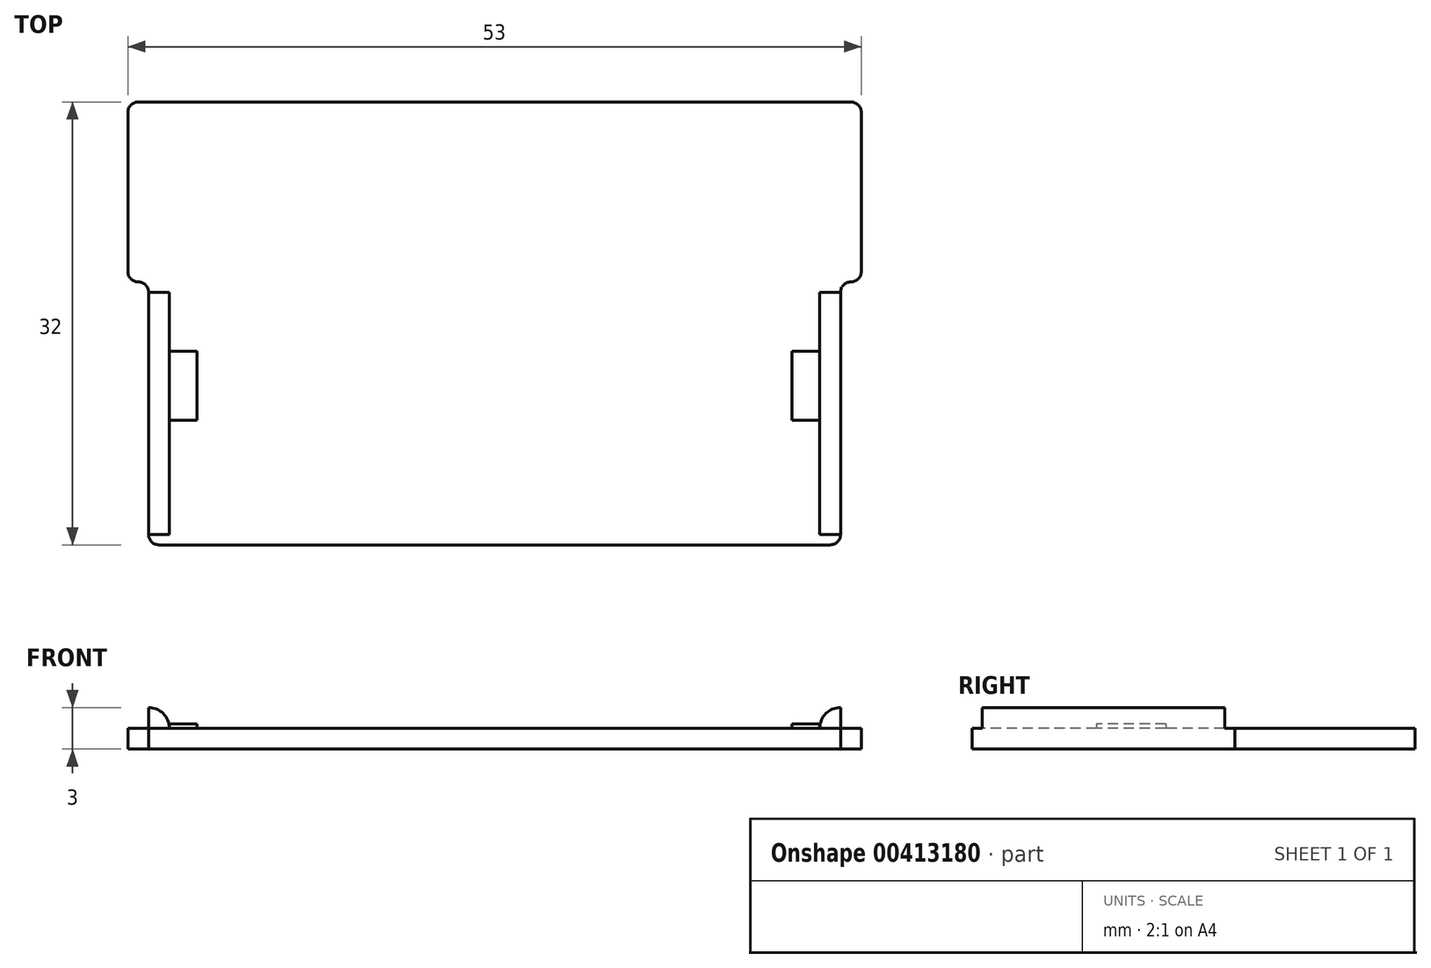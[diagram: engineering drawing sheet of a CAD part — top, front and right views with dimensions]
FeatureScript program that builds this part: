
annotation { "Feature Type Name" : "Feature", "Feature Type Description" : "" }
export const myFeature = defineFeature(function(context is Context, id is Id, definition is map)
    precondition{}
    {
        {
            var Q0;
            Q0=qCreatedBy(makeId("Top.planeOp"),FACE);
            var sketch = newSketch(context, id + "F0", { "sketchPlane" : qUnion([Q0])});
            skLineSegment(sketch, "E0.bottom", {"start": v(-25, 16) * mm, "end": v(25, 16) * mm});
            skLineSegment(sketch, "E0.top", {"start": v(-25, -16) * mm, "end": v(25, -16) * mm});
            skLineSegment(sketch, "E0.left", {"start": v(-25, 16) * mm, "end": v(-25, -16) * mm});
            skLineSegment(sketch, "E0.right", {"start": v(25, 16) * mm, "end": v(25, -16) * mm});
            skPoint(sketch, "E0.middle", {"position": v(0, 0) * mm});
            skLineSegment(sketch, "E1.bottom", {"start": v(-26.5, 16) * mm, "end": v(26.5, 16) * mm});
            skLineSegment(sketch, "E1.top", {"start": v(-26.5, 3) * mm, "end": v(26.5, 3) * mm});
            skLineSegment(sketch, "E1.left", {"start": v(-26.5, 16) * mm, "end": v(-26.5, 3) * mm});
            skLineSegment(sketch, "E1.right", {"start": v(26.5, 16) * mm, "end": v(26.5, 3) * mm});
            skSolve(sketch);
        }
        {
            var Q0;
            {var subQ0=sQuery(id+"F0.wireOp",EDGE,"E0.top");Q0=makeQuery(id+"F0.imprint","IMPRINT",FACE,{"disambiguationData":[TD([[makeQuery(id+"F0.imprint","IMPRINT",EDGE,{"derivedFrom":subQ0}),1.0]])]});}
            var Q1;
            {var subQ0=sQuery(id+"F0.wireOp",EDGE,"E1.bottom");var subQ1=sQuery(id+"F0.wireOp",EDGE,"E0.left");var subQ2=makeQuery(id+"F0.imprint","INTERSECT",VERTEX,{"derivedFrom":[subQ1,subQ0]});Q1=makeQuery(id+"F0.imprint","IMPRINT",FACE,{"disambiguationData":[TD([[makeQuery(id+"F0.imprint","IMPRINT",EDGE,{"disambiguationData":[TD([[subQ2,-1.0]])],"derivedFrom":subQ1}),1.0]])]});}
            var Q2;
            {var subQ5=sQuery(id+"F0.wireOp",EDGE,"E1.left");Q2=makeQuery(id+"F0.imprint","IMPRINT",FACE,{"disambiguationData":[TD([[makeQuery(id+"F0.imprint","IMPRINT",EDGE,{"derivedFrom":subQ5}),1.0]])]});}
            var Q3;
            {var subQ5=sQuery(id+"F0.wireOp",EDGE,"E1.right");Q3=makeQuery(id+"F0.imprint","IMPRINT",FACE,{"disambiguationData":[TD([[makeQuery(id+"F0.imprint","IMPRINT",EDGE,{"derivedFrom":subQ5}),-1.0]])]});}
            extrude(context, id + "F1", {"entities" : qUnion([Q0, Q1, Q2, Q3]), "depth" : 1.5 * mm});
        }
        {
            var Q0;
            Q0=makeQuery(id+"F1.opExtrude","SWEPT_EDGE",EDGE,{"disambiguationData":[OSD([sQuery(id+"F0.wireOp",EDGE,"E1.bottom"),sQuery(id+"F0.wireOp",EDGE,"E1.left")])]});
            var Q1;
            Q1=makeQuery(id+"F1.opExtrude","SWEPT_EDGE",EDGE,{"disambiguationData":[OSD([sQuery(id+"F0.wireOp",EDGE,"E1.top"),sQuery(id+"F0.wireOp",EDGE,"E1.left")])]});
            var Q2;
            Q2=makeQuery(id+"F1.opExtrude","SWEPT_EDGE",EDGE,{"disambiguationData":[OSD([sQuery(id+"F0.wireOp",EDGE,"E0.left"),sQuery(id+"F0.wireOp",EDGE,"E1.top")])]});
            var Q3;
            Q3=makeQuery(id+"F1.opExtrude","SWEPT_EDGE",EDGE,{"disambiguationData":[OSD([sQuery(id+"F0.wireOp",EDGE,"E0.top"),sQuery(id+"F0.wireOp",EDGE,"E0.left")])]});
            var Q4;
            Q4=makeQuery(id+"F1.opExtrude","SWEPT_EDGE",EDGE,{"disambiguationData":[OSD([sQuery(id+"F0.wireOp",EDGE,"E0.top"),sQuery(id+"F0.wireOp",EDGE,"E0.right")])]});
            var Q5;
            Q5=makeQuery(id+"F1.opExtrude","SWEPT_EDGE",EDGE,{"disambiguationData":[OSD([sQuery(id+"F0.wireOp",EDGE,"E0.right"),sQuery(id+"F0.wireOp",EDGE,"E1.top")])]});
            var Q6;
            Q6=makeQuery(id+"F1.opExtrude","SWEPT_EDGE",EDGE,{"disambiguationData":[OSD([sQuery(id+"F0.wireOp",EDGE,"E1.top"),sQuery(id+"F0.wireOp",EDGE,"E1.right")])]});
            var Q7;
            Q7=makeQuery(id+"F1.opExtrude","SWEPT_EDGE",EDGE,{"disambiguationData":[OSD([sQuery(id+"F0.wireOp",EDGE,"E1.bottom"),sQuery(id+"F0.wireOp",EDGE,"E1.right")])]});
            fillet(context, id + "F2", {"entities" : qUnion([Q0, Q1, Q2, Q3, Q4, Q5, Q6, Q7]), "radius" : .75 * mm, "tangentPropagation" : true, "allowEdgeOverflow" : false});
        }
        {
            var Q0;
            Q0=makeQuery(id+"F1.opExtrude","CAP_FACE",FACE,{"disambiguationData":[OSD([sQuery(id+"F0.wireOp",EDGE,"E0.top"),sQuery(id+"F0.wireOp",EDGE,"E0.left"),sQuery(id+"F0.wireOp",EDGE,"E0.right"),sQuery(id+"F0.wireOp",EDGE,"E1.bottom"),sQuery(id+"F0.wireOp",EDGE,"E1.top"),sQuery(id+"F0.wireOp",EDGE,"E1.left"),sQuery(id+"F0.wireOp",EDGE,"E1.right")])],"isStart":false});
            var sketch = newSketch(context, id + "F3", { "sketchPlane" : qUnion([Q0])});
            skLineSegment(sketch, "E2.bottom", {"start": v(-25, 2.25) * mm, "end": v(-23.5, 2.25) * mm});
            skLineSegment(sketch, "E2.left", {"start": v(-25, 2.25) * mm, "end": v(-25, -15.25) * mm});
            skLineSegment(sketch, "E2.right", {"start": v(-23.5, 2.25) * mm, "end": v(-23.5, -15.25) * mm});
            skLineSegment(sketch, "E3.bottom", {"start": v(-23.5, -2) * mm, "end": v(-21.5, -2) * mm});
            skLineSegment(sketch, "E3.top", {"start": v(-23.5, -7) * mm, "end": v(-21.5, -7) * mm});
            skLineSegment(sketch, "E3.left", {"start": v(-23.5, -2) * mm, "end": v(-23.5, -7) * mm});
            skLineSegment(sketch, "E3.right", {"start": v(-21.5, -2) * mm, "end": v(-21.5, -7) * mm});
            skLineSegment(sketch, "E4", {"start": v(0, 4.86) * mm, "end": v(0, -4.8) * mm, "construction": true});
            skLineSegment(sketch, "E5.MirrorCS", {"start": v(25, 2.25) * mm, "end": v(23.5, 2.25) * mm});
            skLineSegment(sketch, "E6.MirrorCS", {"start": v(23.5, 2.25) * mm, "end": v(23.5, -15.25) * mm});
            skLineSegment(sketch, "E7.MirrorCS", {"start": v(23.5, -2) * mm, "end": v(21.5, -2) * mm});
            skLineSegment(sketch, "E8.MirrorCS", {"start": v(21.5, -2) * mm, "end": v(21.5, -7) * mm});
            skLineSegment(sketch, "E9.MirrorCS", {"start": v(23.5, -7) * mm, "end": v(21.5, -7) * mm});
            skLineSegment(sketch, "E10.MirrorCS", {"start": v(25, -15.25) * mm, "end": v(23.5, -15.25) * mm});
            skLineSegment(sketch, "E11.MirrorCS", {"start": v(25, 2.25) * mm, "end": v(25, -15.25) * mm});
            skLineSegment(sketch, "E12", {"start": v(-23.5, -15.25) * mm, "end": v(-25, -15.25) * mm});
            skSolve(sketch);
        }
        {
            var Q0;
            {var subQ1=sQuery(id+"F3.wireOp",EDGE,"E2.bottom");Q0=makeQuery(id+"F3.imprint","IMPRINT",FACE,{"disambiguationData":[TD([[makeQuery(id+"F3.imprint","IMPRINT",EDGE,{"derivedFrom":subQ1}),-1.0]])]});}
            var Q1;
            {var subQ4=sQuery(id+"F3.wireOp",EDGE,"E5.MirrorCS");Q1=makeQuery(id+"F3.imprint","IMPRINT",FACE,{"disambiguationData":[TD([[makeQuery(id+"F3.imprint","IMPRINT",EDGE,{"derivedFrom":subQ4}),1.0]])]});}
            extrude(context, id + "F4", {"entities" : qUnion([Q0, Q1]), "operationType" : NewBodyOperationType.ADD, "depth" : 1.5 * mm});
        }
        {
            var Q0;
            Q0=makeQuery(id+"F4.opExtrude","CAP_EDGE",EDGE,{"disambiguationData":[OSD([sQuery(id+"F3.wireOp",EDGE,"E2.right"),sQuery(id+"F3.wireOp",EDGE,"E3.left")])],"isStart":false});
            var Q1;
            Q1=makeQuery(id+"F4.opExtrude","CAP_EDGE",EDGE,{"disambiguationData":[OSD([sQuery(id+"F3.wireOp",EDGE,"E6.MirrorCS")])],"isStart":false});
            fillet(context, id + "F5", {"entities" : qUnion([Q0, Q1]), "radius" : 1.5 * mm, "tangentPropagation" : true, "allowEdgeOverflow" : false});
        }
        {
            var Q0;
            Q0=makeQuery(id+"F3.imprint","IMPRINT",FACE,{"disambiguationData":[TD([[makeQuery(id+"F3.imprint","IMPRINT",EDGE,{"derivedFrom":sQuery(id+"F3.wireOp",EDGE,"E3.bottom")}),-1.0]])]});
            var Q1;
            {var subQ0=sQuery(id+"F3.wireOp",EDGE,"E7.MirrorCS");Q1=makeQuery(id+"F3.imprint","IMPRINT",FACE,{"disambiguationData":[TD([[makeQuery(id+"F3.imprint","IMPRINT",EDGE,{"derivedFrom":subQ0}),1.0]])]});}
            extrude(context, id + "F6", {"entities" : qUnion([Q0, Q1]), "operationType" : NewBodyOperationType.ADD, "depth" : .3 * mm});
        }
    });
